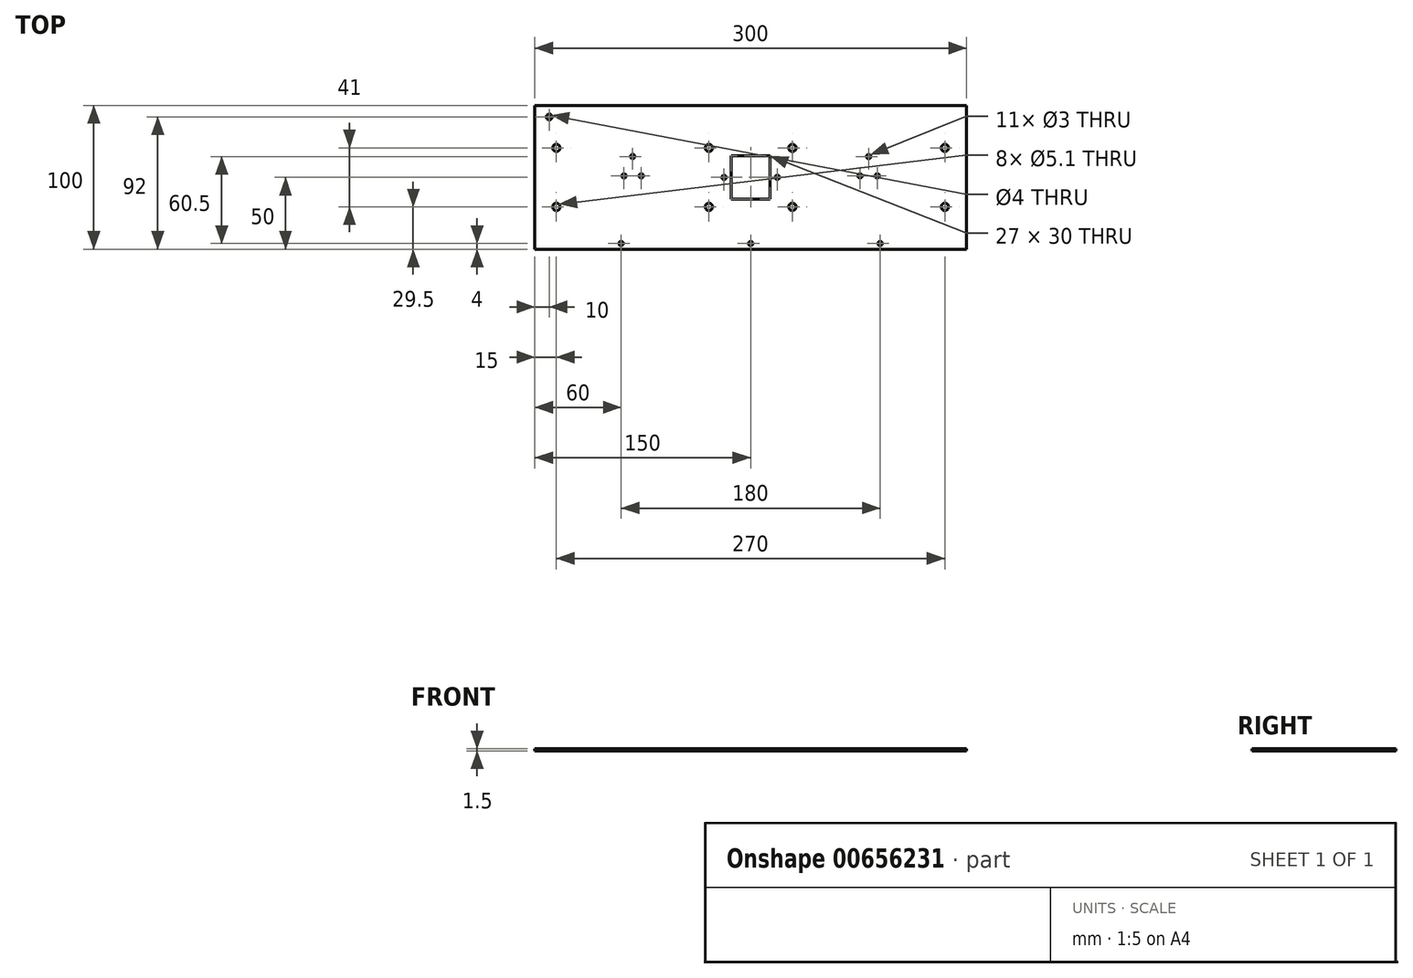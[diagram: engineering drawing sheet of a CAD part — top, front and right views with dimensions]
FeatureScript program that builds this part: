
annotation { "Feature Type Name" : "Feature", "Feature Type Description" : "" }
export const myFeature = defineFeature(function(context is Context, id is Id, definition is map)
    precondition{}
    {
        {
            var Q0;
            Q0=qCreatedBy(makeId("Top.planeOp"),FACE);
            var sketch = newSketch(context, id + "F0", { "sketchPlane" : qUnion([Q0])});
            skLineSegment(sketch, "E0.bottom", {"start": v(0, 0) * mm, "end": v(300, 0) * mm});
            skLineSegment(sketch, "E0.top", {"start": v(0, 100) * mm, "end": v(300, 100) * mm});
            skLineSegment(sketch, "E0.left", {"start": v(0, 0) * mm, "end": v(0, 100) * mm});
            skLineSegment(sketch, "E0.right", {"start": v(300, 0) * mm, "end": v(300, 100) * mm});
            skCircle(sketch, "E1", {"center": v(10, 92) * mm, "radius": 2 * mm});
            skLineSegment(sketch, "E2", {"start": v(10, 92) * mm, "end": v(10, 100) * mm, "construction": true});
            skLineSegment(sketch, "E3", {"start": v(10, 92) * mm, "end": v(0, 92) * mm, "construction": true});
            skLineSegment(sketch, "E4.bottom", {"start": v(136.5, 65) * mm, "end": v(163.5, 65) * mm});
            skLineSegment(sketch, "E4.top", {"start": v(136.5, 35) * mm, "end": v(163.5, 35) * mm});
            skLineSegment(sketch, "E4.left", {"start": v(136.5, 65) * mm, "end": v(136.5, 35) * mm});
            skLineSegment(sketch, "E4.right", {"start": v(163.5, 65) * mm, "end": v(163.5, 35) * mm});
            skCircle(sketch, "E5", {"center": v(60, 4) * mm, "radius": 1.5 * mm});
            skCircle(sketch, "E6", {"center": v(150, 4) * mm, "radius": 1.5 * mm});
            skCircle(sketch, "E7", {"center": v(240, 4) * mm, "radius": 1.5 * mm});
            skCircle(sketch, "E8", {"center": v(131.5, 50) * mm, "radius": 1.5 * mm});
            skCircle(sketch, "E9", {"center": v(168.5, 50) * mm, "radius": 1.5 * mm});
            skCircle(sketch, "E10", {"center": v(15, 70.5) * mm, "radius": 2.55 * mm});
            skCircle(sketch, "E11", {"center": v(15, 29.5) * mm, "radius": 2.55 * mm});
            skCircle(sketch, "E12", {"center": v(121, 29.5) * mm, "radius": 2.55 * mm});
            skCircle(sketch, "E13", {"center": v(121, 70.5) * mm, "radius": 2.55 * mm});
            skCircle(sketch, "E14", {"center": v(179, 70.5) * mm, "radius": 2.55 * mm});
            skCircle(sketch, "E15", {"center": v(179, 29.5) * mm, "radius": 2.55 * mm});
            skCircle(sketch, "E16", {"center": v(285, 29.5) * mm, "radius": 2.55 * mm});
            skCircle(sketch, "E17", {"center": v(285, 70.5) * mm, "radius": 2.55 * mm});
            skLineSegment(sketch, "E18", {"start": v(15, 70.5) * mm, "end": v(121, 70.5) * mm, "construction": true});
            skLineSegment(sketch, "E19", {"start": v(179, 70.5) * mm, "end": v(285, 70.5) * mm, "construction": true});
            skLineSegment(sketch, "E20", {"start": v(68, 70.5) * mm, "end": v(68, 64.5) * mm, "construction": true});
            skCircle(sketch, "E21", {"center": v(68, 64.5) * mm, "radius": 1.5 * mm});
            skLineSegment(sketch, "E22", {"start": v(232, 70.5) * mm, "end": v(232, 64.5) * mm, "construction": true});
            skCircle(sketch, "E23", {"center": v(232, 64.5) * mm, "radius": 1.5 * mm});
            skLineSegment(sketch, "E24", {"start": v(68, 64.5) * mm, "end": v(68, 51) * mm, "construction": true});
            skLineSegment(sketch, "E25", {"start": v(232, 64.5) * mm, "end": v(232, 51) * mm, "construction": true});
            skLineSegment(sketch, "E26", {"start": v(68, 51) * mm, "end": v(74, 51) * mm, "construction": true});
            skLineSegment(sketch, "E27", {"start": v(68, 51) * mm, "end": v(62, 51) * mm, "construction": true});
            skLineSegment(sketch, "E28", {"start": v(232, 51) * mm, "end": v(238, 51) * mm, "construction": true});
            skLineSegment(sketch, "E29", {"start": v(232, 51) * mm, "end": v(226, 51) * mm, "construction": true});
            skCircle(sketch, "E30", {"center": v(62, 51) * mm, "radius": 1.5 * mm});
            skCircle(sketch, "E31", {"center": v(74, 51) * mm, "radius": 1.5 * mm});
            skCircle(sketch, "E32", {"center": v(226, 51) * mm, "radius": 1.5 * mm});
            skCircle(sketch, "E33", {"center": v(238, 51) * mm, "radius": 1.5 * mm});
            skSolve(sketch);
        }
        {
            var Q0;
            Q0=makeQuery(id+"F0.imprint","IMPRINT",FACE,{"disambiguationData":[TD([[makeQuery(id+"F0.imprint","IMPRINT",EDGE,{"derivedFrom":sQuery(id+"F0.wireOp",EDGE,"E0.bottom")}),1.0]])]});
            extrude(context, id + "F1", {"entities" : qUnion([Q0]), "oppositeDirection" : true, "depth" : 1.5 * mm, "offsetDistance" : 25 * mm});
        }
    });
